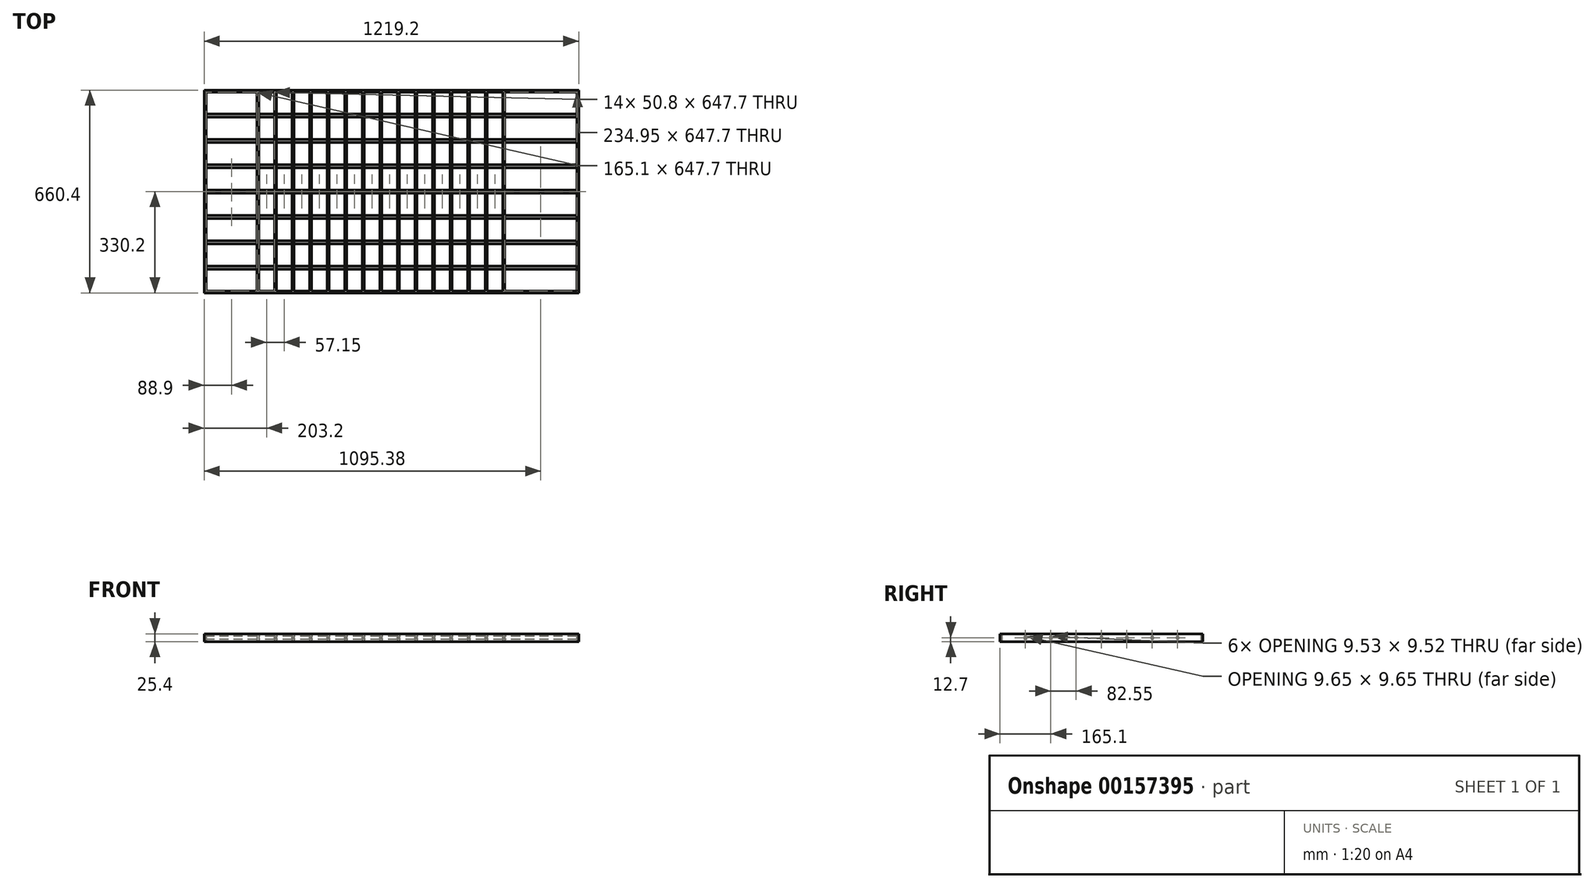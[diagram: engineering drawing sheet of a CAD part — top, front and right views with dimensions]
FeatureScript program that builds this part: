
annotation { "Feature Type Name" : "Feature", "Feature Type Description" : "" }
export const myFeature = defineFeature(function(context is Context, id is Id, definition is map)
    precondition{}
    {
        {
            var Q0;
            Q0=qCreatedBy(makeId("Top.planeOp"),FACE);
            var sketch = newSketch(context, id + "F0", { "sketchPlane" : qUnion([Q0])});
            skLineSegment(sketch, "E0.bottom", {"start": v(609.6, 330.2) * mm, "end": v(-609.6, 330.2) * mm});
            skLineSegment(sketch, "E0.top", {"start": v(609.6, -330.2) * mm, "end": v(-609.6, -330.2) * mm});
            skLineSegment(sketch, "E0.left", {"start": v(609.6, 330.2) * mm, "end": v(609.6, -330.2) * mm});
            skLineSegment(sketch, "E0.right", {"start": v(-609.6, 330.2) * mm, "end": v(-609.6, -330.2) * mm});
            skPoint(sketch, "E0.middle", {"position": v(0, 0) * mm});
            skLineSegment(sketch, "E1.bottom", {"start": v(603.25, 323.85) * mm, "end": v(-603.25, 323.85) * mm});
            skLineSegment(sketch, "E1.top", {"start": v(603.25, -323.85) * mm, "end": v(-603.25, -323.85) * mm});
            skLineSegment(sketch, "E1.left", {"start": v(603.25, 323.85) * mm, "end": v(603.25, -323.85) * mm});
            skLineSegment(sketch, "E1.right", {"start": v(-603.25, 323.85) * mm, "end": v(-603.25, -323.85) * mm});
            skLineSegment(sketch, "E2.bottom", {"start": v(-552.45, 323.85) * mm, "end": v(599.47, 323.85) * mm});
            skLineSegment(sketch, "E2.top", {"start": v(-546.1, -323.85) * mm, "end": v(476.25, -323.85) * mm});
            skLineSegment(sketch, "E3.bottom", {"start": v(546.1, 323.85) * mm, "end": v(-546.1, 323.85) * mm});
            skLineSegment(sketch, "E3.top", {"start": v(546.1, -323.85) * mm, "end": v(539.75, -323.85) * mm});
            skLineSegment(sketch, "E4.bottom", {"start": v(-501.65, -323.85) * mm, "end": v(76.2, -323.85) * mm});
            skLineSegment(sketch, "E4.top", {"start": v(-450.85, 323.85) * mm, "end": v(501.65, 323.85) * mm});
            skLineSegment(sketch, "E5.bottom", {"start": v(-488.95, 323.85) * mm, "end": v(-450.85, 323.85) * mm});
            skLineSegment(sketch, "E5.top", {"start": v(-501.65, -323.85) * mm, "end": v(-495.3, -323.85) * mm});
            skLineSegment(sketch, "E6.bottom", {"start": v(-488.95, 323.85) * mm, "end": v(-381, 323.85) * mm});
            skLineSegment(sketch, "E6.top", {"start": v(-495.3, -323.85) * mm, "end": v(-381, -323.85) * mm});
            skLineSegment(sketch, "E6.right", {"start": v(-381, 323.85) * mm, "end": v(-381, -323.85) * mm});
            skLineSegment(sketch, "E7.bottom", {"start": v(-374.65, 323.85) * mm, "end": v(-323.85, 323.85) * mm});
            skLineSegment(sketch, "E7.top", {"start": v(-374.65, -323.85) * mm, "end": v(-323.85, -323.85) * mm});
            skLineSegment(sketch, "E7.left", {"start": v(-374.65, 323.85) * mm, "end": v(-374.65, -323.85) * mm});
            skLineSegment(sketch, "E7.right", {"start": v(-323.85, 323.85) * mm, "end": v(-323.85, -323.85) * mm});
            skLineSegment(sketch, "E8.bottom", {"start": v(-317.5, 323.85) * mm, "end": v(-266.7, 323.85) * mm});
            skLineSegment(sketch, "E8.top", {"start": v(-317.5, -330.2) * mm, "end": v(-266.7, -330.2) * mm});
            skLineSegment(sketch, "E8.left", {"start": v(-317.5, 323.85) * mm, "end": v(-317.5, -330.2) * mm});
            skLineSegment(sketch, "E8.right", {"start": v(-266.7, 323.85) * mm, "end": v(-266.7, -330.2) * mm});
            skLineSegment(sketch, "E9.bottom", {"start": v(-260.35, 323.85) * mm, "end": v(-209.55, 323.85) * mm});
            skLineSegment(sketch, "E9.top", {"start": v(-260.35, -323.85) * mm, "end": v(-209.55, -323.85) * mm});
            skLineSegment(sketch, "E9.left", {"start": v(-260.35, 323.85) * mm, "end": v(-260.35, -323.85) * mm});
            skLineSegment(sketch, "E9.right", {"start": v(-209.55, 323.85) * mm, "end": v(-209.55, -323.85) * mm});
            skLineSegment(sketch, "E10.bottom", {"start": v(-203.2, 323.85) * mm, "end": v(-152.4, 323.85) * mm});
            skLineSegment(sketch, "E10.top", {"start": v(-203.2, -323.85) * mm, "end": v(-152.4, -323.85) * mm});
            skLineSegment(sketch, "E10.left", {"start": v(-203.2, 323.85) * mm, "end": v(-203.2, -323.85) * mm});
            skLineSegment(sketch, "E10.right", {"start": v(-152.4, 323.85) * mm, "end": v(-152.4, -323.85) * mm});
            skLineSegment(sketch, "E11.bottom", {"start": v(-146.05, 323.85) * mm, "end": v(-95.25, 323.85) * mm});
            skLineSegment(sketch, "E11.top", {"start": v(-146.05, -323.85) * mm, "end": v(-95.25, -323.85) * mm});
            skLineSegment(sketch, "E11.left", {"start": v(-146.05, 323.85) * mm, "end": v(-146.05, -323.85) * mm});
            skLineSegment(sketch, "E11.right", {"start": v(-95.25, 323.85) * mm, "end": v(-95.25, -323.85) * mm});
            skLineSegment(sketch, "E12.bottom", {"start": v(-88.9, 323.85) * mm, "end": v(-38.1, 323.85) * mm});
            skLineSegment(sketch, "E12.top", {"start": v(-88.9, -323.85) * mm, "end": v(-38.1, -323.85) * mm});
            skLineSegment(sketch, "E12.left", {"start": v(-88.9, 323.85) * mm, "end": v(-88.9, -323.85) * mm});
            skLineSegment(sketch, "E12.right", {"start": v(-38.1, 323.85) * mm, "end": v(-38.1, -323.85) * mm});
            skLineSegment(sketch, "E13.bottom", {"start": v(-31.75, 323.85) * mm, "end": v(19.05, 323.85) * mm});
            skLineSegment(sketch, "E13.top", {"start": v(-31.75, -323.85) * mm, "end": v(19.05, -323.85) * mm});
            skLineSegment(sketch, "E13.left", {"start": v(-31.75, 323.85) * mm, "end": v(-31.75, -323.85) * mm});
            skLineSegment(sketch, "E13.right", {"start": v(19.05, 323.85) * mm, "end": v(19.05, -323.85) * mm});
            skLineSegment(sketch, "E14.bottom", {"start": v(25.4, 323.85) * mm, "end": v(76.2, 323.85) * mm});
            skLineSegment(sketch, "E14.top", {"start": v(25.4, -323.85) * mm, "end": v(76.2, -323.85) * mm});
            skLineSegment(sketch, "E14.left", {"start": v(25.4, 323.85) * mm, "end": v(25.4, -323.85) * mm});
            skLineSegment(sketch, "E14.right", {"start": v(76.2, 323.85) * mm, "end": v(76.2, -323.85) * mm});
            skLineSegment(sketch, "E15.bottom", {"start": v(82.55, 323.85) * mm, "end": v(133.35, 323.85) * mm});
            skLineSegment(sketch, "E15.top", {"start": v(82.55, -323.85) * mm, "end": v(133.35, -323.85) * mm});
            skLineSegment(sketch, "E15.left", {"start": v(82.55, 323.85) * mm, "end": v(82.55, -323.85) * mm});
            skLineSegment(sketch, "E15.right", {"start": v(133.35, 323.85) * mm, "end": v(133.35, -323.85) * mm});
            skLineSegment(sketch, "E16.bottom", {"start": v(139.7, 323.85) * mm, "end": v(190.5, 323.85) * mm});
            skLineSegment(sketch, "E16.top", {"start": v(139.7, -323.85) * mm, "end": v(190.5, -323.85) * mm});
            skLineSegment(sketch, "E16.left", {"start": v(139.7, 323.85) * mm, "end": v(139.7, -323.85) * mm});
            skLineSegment(sketch, "E16.right", {"start": v(190.5, 323.85) * mm, "end": v(190.5, -323.85) * mm});
            skLineSegment(sketch, "E17.bottom", {"start": v(196.85, 323.85) * mm, "end": v(247.65, 323.85) * mm});
            skLineSegment(sketch, "E17.top", {"start": v(196.85, -323.85) * mm, "end": v(247.65, -323.85) * mm});
            skLineSegment(sketch, "E17.left", {"start": v(196.85, 323.85) * mm, "end": v(196.85, -323.85) * mm});
            skLineSegment(sketch, "E17.right", {"start": v(247.65, 323.85) * mm, "end": v(247.65, -323.85) * mm});
            skLineSegment(sketch, "E18.bottom", {"start": v(254, 323.85) * mm, "end": v(304.8, 323.85) * mm});
            skLineSegment(sketch, "E18.top", {"start": v(254, -323.85) * mm, "end": v(304.8, -323.85) * mm});
            skLineSegment(sketch, "E18.left", {"start": v(254, 323.85) * mm, "end": v(254, -323.85) * mm});
            skLineSegment(sketch, "E18.right", {"start": v(304.8, 323.85) * mm, "end": v(304.8, -323.85) * mm});
            skLineSegment(sketch, "E19.bottom", {"start": v(311.15, 323.85) * mm, "end": v(361.95, 323.85) * mm});
            skLineSegment(sketch, "E19.top", {"start": v(311.15, -323.85) * mm, "end": v(361.95, -323.85) * mm});
            skLineSegment(sketch, "E19.left", {"start": v(311.15, 323.85) * mm, "end": v(311.15, -323.85) * mm});
            skLineSegment(sketch, "E19.right", {"start": v(361.95, 323.85) * mm, "end": v(361.95, -323.85) * mm});
            skLineSegment(sketch, "E20.bottom", {"start": v(368.3, 323.85) * mm, "end": v(419.1, 323.85) * mm});
            skLineSegment(sketch, "E20.top", {"start": v(368.3, -323.85) * mm, "end": v(419.1, -323.85) * mm});
            skLineSegment(sketch, "E20.left", {"start": v(368.3, 323.85) * mm, "end": v(368.3, -323.85) * mm});
            skLineSegment(sketch, "E20.right", {"start": v(419.1, 323.85) * mm, "end": v(419.1, -323.85) * mm});
            skLineSegment(sketch, "E21.bottom", {"start": v(419.1, 323.85) * mm, "end": v(425.45, 323.85) * mm});
            skLineSegment(sketch, "E21.top", {"start": v(419.1, -323.85) * mm, "end": v(425.45, -323.85) * mm});
            skLineSegment(sketch, "E21.right", {"start": v(425.45, 323.85) * mm, "end": v(425.45, -323.85) * mm});
            skLineSegment(sketch, "E22.bottom", {"start": v(425.45, 323.85) * mm, "end": v(476.25, 323.85) * mm});
            skLineSegment(sketch, "E22.top", {"start": v(425.45, -323.85) * mm, "end": v(476.25, -323.85) * mm});
            skLineSegment(sketch, "E22.right", {"start": v(476.25, 323.85) * mm, "end": v(476.25, -323.85) * mm});
            skLineSegment(sketch, "E23.bottom", {"start": v(476.25, 323.85) * mm, "end": v(482.6, 323.85) * mm});
            skLineSegment(sketch, "E23.top", {"start": v(476.25, -323.85) * mm, "end": v(482.6, -323.85) * mm});
            skLineSegment(sketch, "E23.right", {"start": v(482.6, 323.85) * mm, "end": v(482.6, -323.85) * mm});
            skLineSegment(sketch, "E24.bottom", {"start": v(482.6, 323.85) * mm, "end": v(533.4, 323.85) * mm});
            skLineSegment(sketch, "E24.top", {"start": v(482.6, -323.85) * mm, "end": v(533.4, -323.85) * mm});
            skLineSegment(sketch, "E24.right", {"start": v(533.4, 323.85) * mm, "end": v(533.4, -323.85) * mm});
            skLineSegment(sketch, "E25.bottom", {"start": v(533.4, 323.85) * mm, "end": v(539.75, 323.85) * mm});
            skLineSegment(sketch, "E25.top", {"start": v(533.4, -323.85) * mm, "end": v(539.75, -323.85) * mm});
            skLineSegment(sketch, "E25.right", {"start": v(539.75, 323.85) * mm, "end": v(539.75, -323.85) * mm});
            skLineSegment(sketch, "E26.bottom", {"start": v(539.75, 323.85) * mm, "end": v(590.55, 323.85) * mm});
            skLineSegment(sketch, "E26.top", {"start": v(539.75, 323.85) * mm, "end": v(590.55, 323.85) * mm});
            skLineSegment(sketch, "E26.left", {"start": v(539.75, 323.85) * mm, "end": v(539.75, 323.85) * mm});
            skLineSegment(sketch, "E26.right", {"start": v(590.55, 323.85) * mm, "end": v(590.55, 323.85) * mm});
            skLineSegment(sketch, "E27.bottom", {"start": v(539.75, 323.85) * mm, "end": v(618.1, 323.85) * mm});
            skLineSegment(sketch, "E27.top", {"start": v(539.75, -323.85) * mm, "end": v(567.3, -323.85) * mm});
            skLineSegment(sketch, "E28.bottom", {"start": v(590.55, 323.85) * mm, "end": v(596.9, 323.85) * mm});
            skLineSegment(sketch, "E28.top", {"start": v(590.55, -323.85) * mm, "end": v(596.9, -323.85) * mm});
            skLineSegment(sketch, "E29.bottom", {"start": v(-438.15, -323.85) * mm, "end": v(-457.2, -323.85) * mm});
            skLineSegment(sketch, "E29.top", {"start": v(-406.4, 323.85) * mm, "end": v(-438.15, 323.85) * mm});
            skLineSegment(sketch, "E29.right", {"start": v(-438.15, -323.85) * mm, "end": v(-438.15, 323.85) * mm});
            skLineSegment(sketch, "E30.bottom", {"start": v(-431.8, -323.85) * mm, "end": v(-488.95, -323.85) * mm});
            skLineSegment(sketch, "E30.top", {"start": v(-431.8, 323.85) * mm, "end": v(-488.95, 323.85) * mm});
            skLineSegment(sketch, "E30.left", {"start": v(-431.8, -323.85) * mm, "end": v(-431.8, 323.85) * mm});
            skLineSegment(sketch, "E30.right", {"start": v(-488.95, -323.85) * mm, "end": v(-488.95, 323.85) * mm});
            skLineSegment(sketch, "E31.bottom", {"start": v(-495.3, -323.85) * mm, "end": v(-546.1, -323.85) * mm});
            skLineSegment(sketch, "E31.top", {"start": v(-495.3, 323.85) * mm, "end": v(-546.1, 323.85) * mm});
            skLineSegment(sketch, "E31.left", {"start": v(-495.3, -323.85) * mm, "end": v(-495.3, 323.85) * mm});
            skLineSegment(sketch, "E31.right", {"start": v(-546.1, -323.85) * mm, "end": v(-546.1, 323.85) * mm});
            skLineSegment(sketch, "E32.bottom", {"start": v(-546.1, 323.85) * mm, "end": v(-552.45, 323.85) * mm});
            skLineSegment(sketch, "E32.left", {"start": v(-546.1, 323.85) * mm, "end": v(-546.1, -323.85) * mm});
            skLineSegment(sketch, "E32.right", {"start": v(-552.45, 323.85) * mm, "end": v(-552.45, -323.85) * mm});
            skLineSegment(sketch, "E33.trimOffspring", {"start": v(533.4, -323.85) * mm, "end": v(-546.1, -323.85) * mm});
            skLineSegment(sketch, "E34.trimOffspring", {"start": v(539.75, -323.85) * mm, "end": v(552.45, -323.85) * mm});
            skLineSegment(sketch, "E35.trimOffspring", {"start": v(425.45, -323.85) * mm, "end": v(450.85, -323.85) * mm});
            skLineSegment(sketch, "E36.trimOffspring", {"start": v(82.55, -323.85) * mm, "end": v(419.1, -323.85) * mm});
            skPoint(sketch, "E37.orphan", {"position": v(-599.47, -323.85) * mm});
            skSolve(sketch);
        }
        {
            var Q0;
            Q0 = qSketchRegion(id + "F0", true);
            var Q1;
            Q1=makeQuery(id+"F0.imprint","IMPRINT",FACE,{"disambiguationData":[TD([[makeQuery(id+"F0.imprint","IMPRINT",EDGE,{"derivedFrom":sQuery(id+"F0.wireOp",EDGE,"E32.bottom")}),1.0]])]});
            var Q2;
            Q2=makeQuery(id+"F0.imprint","IMPRINT",FACE,{"disambiguationData":[TD([[makeQuery(id+"F0.imprint","IMPRINT",EDGE,{"derivedFrom":sQuery(id+"F0.wireOp",EDGE,"E3.bottom")}),1.0]])]});
            var Q3;
            {var subQ0=sQuery(id+"F0.wireOp",EDGE,"E29.right");Q3=makeQuery(id+"F0.imprint","IMPRINT",FACE,{"disambiguationData":[TD([[makeQuery(id+"F0.imprint","IMPRINT",EDGE,{"derivedFrom":subQ0}),-1.0]])]});}
            var Q4;
            {var subQ0=sQuery(id+"F0.wireOp",EDGE,"E6.right");Q4=makeQuery(id+"F0.imprint","IMPRINT",FACE,{"disambiguationData":[TD([[makeQuery(id+"F0.imprint","IMPRINT",EDGE,{"derivedFrom":subQ0}),1.0]])]});}
            var Q5;
            {var subQ0=sQuery(id+"F0.wireOp",EDGE,"E7.right");Q5=makeQuery(id+"F0.imprint","IMPRINT",FACE,{"disambiguationData":[TD([[makeQuery(id+"F0.imprint","IMPRINT",EDGE,{"derivedFrom":subQ0}),1.0]])]});}
            var Q6;
            {var subQ3=sQuery(id+"F0.wireOp",EDGE,"E9.left");Q6=makeQuery(id+"F0.imprint","IMPRINT",FACE,{"disambiguationData":[TD([[makeQuery(id+"F0.imprint","IMPRINT",EDGE,{"derivedFrom":subQ3}),-1.0]])]});}
            var Q7;
            {var subQ0=sQuery(id+"F0.wireOp",EDGE,"E9.right");Q7=makeQuery(id+"F0.imprint","IMPRINT",FACE,{"disambiguationData":[TD([[makeQuery(id+"F0.imprint","IMPRINT",EDGE,{"derivedFrom":subQ0}),1.0]])]});}
            var Q8;
            {var subQ0=sQuery(id+"F0.wireOp",EDGE,"E10.right");Q8=makeQuery(id+"F0.imprint","IMPRINT",FACE,{"disambiguationData":[TD([[makeQuery(id+"F0.imprint","IMPRINT",EDGE,{"derivedFrom":subQ0}),1.0]])]});}
            var Q9;
            {var subQ0=sQuery(id+"F0.wireOp",EDGE,"E11.right");Q9=makeQuery(id+"F0.imprint","IMPRINT",FACE,{"disambiguationData":[TD([[makeQuery(id+"F0.imprint","IMPRINT",EDGE,{"derivedFrom":subQ0}),1.0]])]});}
            var Q10;
            {var subQ0=sQuery(id+"F0.wireOp",EDGE,"E12.right");Q10=makeQuery(id+"F0.imprint","IMPRINT",FACE,{"disambiguationData":[TD([[makeQuery(id+"F0.imprint","IMPRINT",EDGE,{"derivedFrom":subQ0}),1.0]])]});}
            var Q11;
            {var subQ0=sQuery(id+"F0.wireOp",EDGE,"E13.right");Q11=makeQuery(id+"F0.imprint","IMPRINT",FACE,{"disambiguationData":[TD([[makeQuery(id+"F0.imprint","IMPRINT",EDGE,{"derivedFrom":subQ0}),1.0]])]});}
            var Q12;
            {var subQ0=sQuery(id+"F0.wireOp",EDGE,"E14.right");Q12=makeQuery(id+"F0.imprint","IMPRINT",FACE,{"disambiguationData":[TD([[makeQuery(id+"F0.imprint","IMPRINT",EDGE,{"derivedFrom":subQ0}),1.0]])]});}
            var Q13;
            {var subQ0=sQuery(id+"F0.wireOp",EDGE,"E15.right");Q13=makeQuery(id+"F0.imprint","IMPRINT",FACE,{"disambiguationData":[TD([[makeQuery(id+"F0.imprint","IMPRINT",EDGE,{"derivedFrom":subQ0}),1.0]])]});}
            var Q14;
            {var subQ0=sQuery(id+"F0.wireOp",EDGE,"E16.right");Q14=makeQuery(id+"F0.imprint","IMPRINT",FACE,{"disambiguationData":[TD([[makeQuery(id+"F0.imprint","IMPRINT",EDGE,{"derivedFrom":subQ0}),1.0]])]});}
            var Q15;
            {var subQ0=sQuery(id+"F0.wireOp",EDGE,"E17.right");Q15=makeQuery(id+"F0.imprint","IMPRINT",FACE,{"disambiguationData":[TD([[makeQuery(id+"F0.imprint","IMPRINT",EDGE,{"derivedFrom":subQ0}),1.0]])]});}
            var Q16;
            {var subQ0=sQuery(id+"F0.wireOp",EDGE,"E18.right");Q16=makeQuery(id+"F0.imprint","IMPRINT",FACE,{"disambiguationData":[TD([[makeQuery(id+"F0.imprint","IMPRINT",EDGE,{"derivedFrom":subQ0}),1.0]])]});}
            var Q17;
            {var subQ2=sQuery(id+"F0.wireOp",EDGE,"E19.right");Q17=makeQuery(id+"F0.imprint","IMPRINT",FACE,{"disambiguationData":[TD([[makeQuery(id+"F0.imprint","IMPRINT",EDGE,{"derivedFrom":subQ2}),1.0]])]});}
            var Q18;
            Q18=makeQuery(id+"F0.imprint","IMPRINT",FACE,{"disambiguationData":[TD([[makeQuery(id+"F0.imprint","IMPRINT",EDGE,{"derivedFrom":sQuery(id+"F0.wireOp",EDGE,"E21.bottom")}),-1.0]])]});
            var Q19;
            Q19=makeQuery(id+"F0.imprint","IMPRINT",FACE,{"disambiguationData":[TD([[makeQuery(id+"F0.imprint","IMPRINT",EDGE,{"derivedFrom":sQuery(id+"F0.wireOp",EDGE,"E23.bottom")}),-1.0]])]});
            var Q20;
            Q20=makeQuery(id+"F0.imprint","IMPRINT",FACE,{"disambiguationData":[TD([[makeQuery(id+"F0.imprint","IMPRINT",EDGE,{"derivedFrom":sQuery(id+"F0.wireOp",EDGE,"E25.bottom")}),-1.0]])]});
            extrude(context, id + "F1", {"entities" : qUnion([Q0, Q1, Q2, Q3, Q4, Q5, Q6, Q7, Q8, Q9, Q10, Q11, Q12, Q13, Q14, Q15, Q16, Q17, Q18, Q19, Q20]), "depth" : 25.4 * mm});
        }
        {
            var Q0;
            Q0=makeQuery(id+"F1.opExtrude","SWEPT_FACE",FACE,{"disambiguationData":[OSD([sQuery(id+"F0.wireOp",EDGE,"E0.right")])]});
            var sketch = newSketch(context, id + "F2", { "sketchPlane" : qUnion([Q0])});
            skCircle(sketch, "E38", {"center": v(247.65, 12.7) * mm, "radius": 4.83 * mm});
            skCircle(sketch, "E39", {"center": v(165.1, 12.7) * mm, "radius": 4.76 * mm});
            skCircle(sketch, "E40", {"center": v(82.55, 12.7) * mm, "radius": 4.76 * mm});
            skCircle(sketch, "E41", {"center": v(0, 12.7) * mm, "radius": 4.76 * mm});
            skCircle(sketch, "E42", {"center": v(-82.55, 12.7) * mm, "radius": 4.76 * mm});
            skCircle(sketch, "E43", {"center": v(-165.1, 12.7) * mm, "radius": 4.76 * mm});
            skCircle(sketch, "E44", {"center": v(-247.65, 12.7) * mm, "radius": 4.76 * mm});
            skLineSegment(sketch, "E45", {"start": v(-330.2, 12.7) * mm, "end": v(330.2, 12.7) * mm});
            skSolve(sketch);
        }
        {
            var Q0;
            Q0 = qSketchRegion(id + "F2", true);
            extrude(context, id + "F3", {"entities" : qUnion([Q0]), "operationType" : NewBodyOperationType.ADD, "oppositeDirection" : true, "depth" : 1219.2 * mm});
        }
    });
